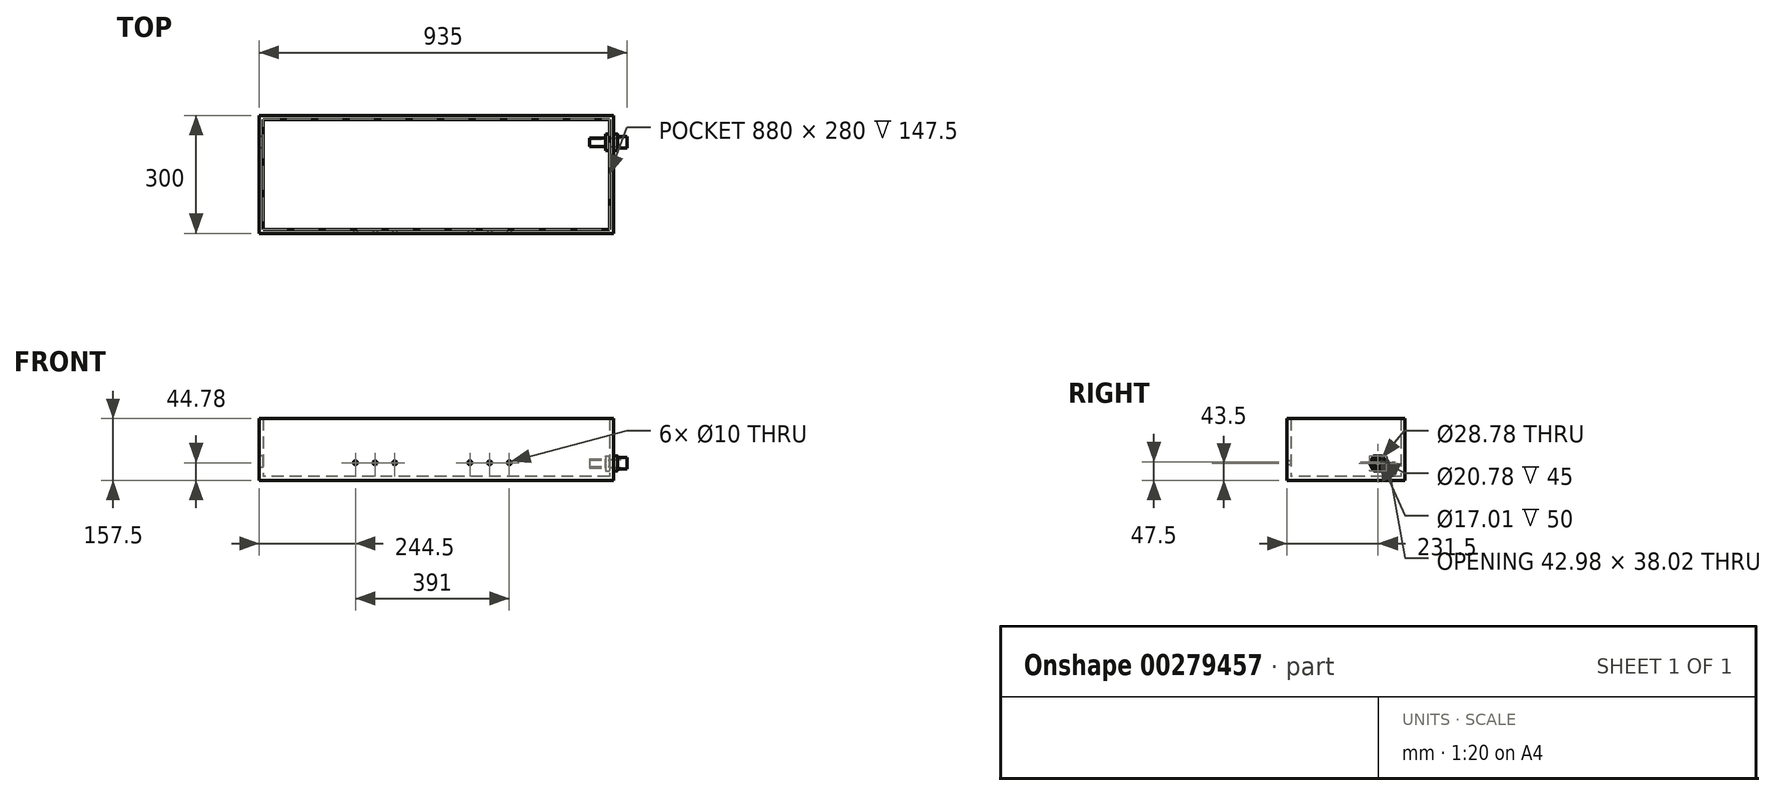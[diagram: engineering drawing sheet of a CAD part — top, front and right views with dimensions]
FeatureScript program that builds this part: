
annotation { "Feature Type Name" : "Feature", "Feature Type Description" : "" }
export const myFeature = defineFeature(function(context is Context, id is Id, definition is map)
    precondition{}
    {
        {
            var Q0;
            Q0=qCreatedBy(makeId("Top.planeOp"),FACE);
            var sketch = newSketch(context, id + "F0", { "sketchPlane" : qUnion([Q0])});
            skLineSegment(sketch, "E0.bottom", {"start": v(450, 150) * mm, "end": v(-450, 150) * mm});
            skLineSegment(sketch, "E0.top", {"start": v(450, -150) * mm, "end": v(-450, -150) * mm});
            skLineSegment(sketch, "E0.left", {"start": v(450, 150) * mm, "end": v(450, -150) * mm});
            skLineSegment(sketch, "E0.right", {"start": v(-450, 150) * mm, "end": v(-450, -150) * mm});
            skPoint(sketch, "E0.middle", {"position": v(0, 0) * mm});
            skSolve(sketch);
        }
        {
            var Q0;
            Q0=qSketchRegion(id+"F0",true);
            extrude(context, id + "F1", {"entities" : qUnion([Q0]), "depth" : 7.5 * mm});
        }
        {
            var Q0;
            Q0=makeQuery(id+"F1.opExtrude","CAP_FACE",FACE,{"disambiguationData":[OSD([sQuery(id+"F0.wireOp",EDGE,"E0.bottom"),sQuery(id+"F0.wireOp",EDGE,"E0.top"),sQuery(id+"F0.wireOp",EDGE,"E0.left"),sQuery(id+"F0.wireOp",EDGE,"E0.right")])],"isStart":false});
            var sketch = newSketch(context, id + "F2", { "sketchPlane" : qUnion([Q0])});
            skLineSegment(sketch, "E1.bottom", {"start": v(442.5, 142.5) * mm, "end": v(-442.5, 142.5) * mm});
            skLineSegment(sketch, "E1.top", {"start": v(442.5, -142.5) * mm, "end": v(-442.5, -142.5) * mm});
            skLineSegment(sketch, "E1.left", {"start": v(442.5, 142.5) * mm, "end": v(442.5, -142.5) * mm});
            skLineSegment(sketch, "E1.right", {"start": v(-442.5, 142.5) * mm, "end": v(-442.5, -142.5) * mm});
            skPoint(sketch, "E1.middle", {"position": v(0, 0) * mm});
            skLineSegment(sketch, "E2.bottom", {"start": v(450, 150) * mm, "end": v(-450, 150) * mm});
            skLineSegment(sketch, "E2.top", {"start": v(450, -150) * mm, "end": v(-450, -150) * mm});
            skLineSegment(sketch, "E2.left", {"start": v(450, 150) * mm, "end": v(450, -150) * mm});
            skLineSegment(sketch, "E2.right", {"start": v(-450, 150) * mm, "end": v(-450, -150) * mm});
            skSolve(sketch);
        }
        {
            var Q0;
            Q0=qSketchRegion(id+"F2",true);
            extrude(context, id + "F3", {"entities" : qUnion([Q0]), "operationType" : NewBodyOperationType.ADD, "depth" : 150 * mm});
        }
        {
            var Q0;
            Q0=makeQuery(id+"F1.opExtrude","CAP_FACE",FACE,{"disambiguationData":[OSD([sQuery(id+"F0.wireOp",EDGE,"E0.bottom"),sQuery(id+"F0.wireOp",EDGE,"E0.top"),sQuery(id+"F0.wireOp",EDGE,"E0.left"),sQuery(id+"F0.wireOp",EDGE,"E0.right")])],"isStart":false});
            extrude(context, id + "F4", {"entities" : qUnion([Q0]), "depth" : 2.5 * mm});
        }
        {
            var Q0;
            Q0=makeQuery(id+"F4.opExtrude","CAP_FACE",FACE,{"disambiguationData":[OSD([sQuery(id+"F0.wireOp",EDGE,"E0.bottom"),sQuery(id+"F0.wireOp",EDGE,"E0.top"),sQuery(id+"F0.wireOp",EDGE,"E0.left"),sQuery(id+"F0.wireOp",EDGE,"E0.right")])],"isStart":false});
            var sketch = newSketch(context, id + "F5", { "sketchPlane" : qUnion([Q0])});
            skLineSegment(sketch, "E3.bottom", {"start": v(442.5, 142.5) * mm, "end": v(-442.5, 142.5) * mm});
            skLineSegment(sketch, "E3.top", {"start": v(442.5, -142.5) * mm, "end": v(-442.5, -142.5) * mm});
            skLineSegment(sketch, "E3.left", {"start": v(442.5, 142.5) * mm, "end": v(442.5, -142.5) * mm});
            skLineSegment(sketch, "E3.right", {"start": v(-442.5, 142.5) * mm, "end": v(-442.5, -142.5) * mm});
            skPoint(sketch, "E3.middle", {"position": v(0, 0) * mm});
            skLineSegment(sketch, "E4.bottom", {"start": v(440, 140) * mm, "end": v(-440, 140) * mm});
            skLineSegment(sketch, "E4.top", {"start": v(440, -140) * mm, "end": v(-440, -140) * mm});
            skLineSegment(sketch, "E4.left", {"start": v(440, 140) * mm, "end": v(440, -140) * mm});
            skLineSegment(sketch, "E4.right", {"start": v(-440, 140) * mm, "end": v(-440, -140) * mm});
            skSolve(sketch);
        }
        {
            var Q0;
            Q0=qSketchRegion(id+"F5",true);
            extrude(context, id + "F6", {"entities" : qUnion([Q0]), "operationType" : NewBodyOperationType.ADD, "depth" : 147.5 * mm});
        }
        {
            var Q0;
            Q0=makeQuery(id+"F3.boolean.opBoolean","MERGE",FACE,{"derivedFrom":[makeQuery(id+"F1.opExtrude","SWEPT_FACE",FACE,{"disambiguationData":[OSD([sQuery(id+"F0.wireOp",EDGE,"E0.top")])]}),makeQuery(id+"F3.opExtrude","SWEPT_FACE",FACE,{"disambiguationData":[OSD([sQuery(id+"F2.wireOp",EDGE,"E2.top")])]})]});
            var sketch = newSketch(context, id + "F7", { "sketchPlane" : qUnion([Q0])});
            skLineSegment(sketch, "E5.bottom", {"start": v(354.25, 147.22) * mm, "end": v(-354.25, 147.22) * mm, "construction": true});
            skLineSegment(sketch, "E5.top", {"start": v(354.25, 15) * mm, "end": v(-354.25, 15) * mm, "construction": true});
            skLineSegment(sketch, "E5.left", {"start": v(354.25, 147.22) * mm, "end": v(354.25, 15) * mm, "construction": true});
            skLineSegment(sketch, "E5.right", {"start": v(-354.25, 147.22) * mm, "end": v(-354.25, 15) * mm, "construction": true});
            skPoint(sketch, "E5.middle", {"position": v(0, 78.75) * mm});
            skPoint(sketch, "E5.middle.positionSnap0", {"position": v(-450, 78.75) * mm});
            skPoint(sketch, "E5.centerSnap0", {"position": v(-450, 78.75) * mm});
            skCircle(sketch, "E6", {"center": v(85.5, 44.78) * mm, "radius": 5 * mm});
            skLineSegment(sketch, "E7", {"start": v(85.5, 44.78) * mm, "end": v(85.5, 15) * mm, "construction": true});
            skLineSegment(sketch, "E8", {"start": v(85.5, 44.78) * mm, "end": v(354.25, 44.78) * mm, "construction": true});
            skCircle(sketch, "E9.1.0.0", {"center": v(135.5, 44.78) * mm, "radius": 5 * mm});
            skLineSegment(sketch, "E9.direction1", {"start": v(85.5, 44.78) * mm, "end": v(135.5, 44.78) * mm, "construction": true});
            skCircle(sketch, "E10", {"center": v(-105.5, 44.78) * mm, "radius": 5 * mm});
            skLineSegment(sketch, "E11", {"start": v(-105.5, 15) * mm, "end": v(-105.5, 44.78) * mm, "construction": true});
            skLineSegment(sketch, "E12", {"start": v(-105.5, 44.78) * mm, "end": v(-354.25, 44.78) * mm, "construction": true});
            skCircle(sketch, "E13.1.0.0", {"center": v(-155.5, 44.78) * mm, "radius": 5 * mm});
            skLineSegment(sketch, "E13.direction1", {"start": v(-105.5, 44.78) * mm, "end": v(-155.5, 44.78) * mm, "construction": true});
            skCircle(sketch, "E14.0.2.0", {"center": v(185.5, 44.78) * mm, "radius": 5 * mm});
            skCircle(sketch, "E15.0.2.0", {"center": v(-205.5, 44.78) * mm, "radius": 5 * mm});
            skSolve(sketch);
        }
        {
            var Q0;
            Q0=qSketchRegion(id+"F7",true);
            extrude(context, id + "F8", {"entities" : qUnion([Q0]), "operationType" : NewBodyOperationType.REMOVE, "oppositeDirection" : true, "depth" : 25 * mm});
        }
        {
            var Q0;
            Q0=makeQuery(id+"F3.boolean.opBoolean","MERGE",FACE,{"derivedFrom":[makeQuery(id+"F1.opExtrude","SWEPT_FACE",FACE,{"disambiguationData":[OSD([sQuery(id+"F0.wireOp",EDGE,"E0.right")])]}),makeQuery(id+"F3.opExtrude","SWEPT_FACE",FACE,{"disambiguationData":[OSD([sQuery(id+"F2.wireOp",EDGE,"E2.right")])]})]});
            var sketch = newSketch(context, id + "F9", { "sketchPlane" : qUnion([Q0])});
            skCircle(sketch, "E16", {"center": v(-81.5, 47.5) * mm, "radius": 14.4 * mm});
            skLineSegment(sketch, "E17", {"start": v(-81.5, 47.5) * mm, "end": v(-81.5, 0) * mm, "construction": true});
            skLineSegment(sketch, "E18", {"start": v(-81.5, 47.5) * mm, "end": v(-150, 47.5) * mm, "construction": true});
            skSolve(sketch);
        }
        {
            var Q0;
            Q0 = qSketchRegion(id + "F9", true);
            extrude(context, id + "F10", {"entities" : qUnion([Q0]), "operationType" : NewBodyOperationType.REMOVE, "oppositeDirection" : true, "depth" : 500 * mm});
        }
        {
            var Q0;
            Q0=makeQuery(id+"F3.boolean.opBoolean","MERGE",FACE,{"derivedFrom":[makeQuery(id+"F1.opExtrude","SWEPT_FACE",FACE,{"disambiguationData":[OSD([sQuery(id+"F0.wireOp",EDGE,"E0.left")])]}),makeQuery(id+"F3.opExtrude","SWEPT_FACE",FACE,{"disambiguationData":[OSD([sQuery(id+"F2.wireOp",EDGE,"E2.left")])]})]});
            var sketch = newSketch(context, id + "F11", { "sketchPlane" : qUnion([Q0])});
            skCircle(sketch, "E19", {"center": v(81.5, 43.5) * mm, "radius": 14.4 * mm});
            skLineSegment(sketch, "E20", {"start": v(81.5, 0) * mm, "end": v(81.5, 43.5) * mm, "construction": true});
            skLineSegment(sketch, "E21", {"start": v(150, 43.5) * mm, "end": v(81.5, 43.5) * mm, "construction": true});
            skSolve(sketch);
        }
        {
            var Q0;
            Q0 = qSketchRegion(id + "F11", true);
            extrude(context, id + "F12", {"entities" : qUnion([Q0]), "operationType" : NewBodyOperationType.REMOVE, "oppositeDirection" : true, "depth" : 25 * mm});
        }
        {
            var Q0;
            Q0=makeQuery(id+"F3.boolean.opBoolean","MERGE",FACE,{"derivedFrom":[makeQuery(id+"F1.opExtrude","SWEPT_FACE",FACE,{"disambiguationData":[OSD([sQuery(id+"F0.wireOp",EDGE,"E0.left")])]}),makeQuery(id+"F3.opExtrude","SWEPT_FACE",FACE,{"disambiguationData":[OSD([sQuery(id+"F2.wireOp",EDGE,"E2.left")])]})]});
            var sketch = newSketch(context, id + "F13", { "sketchPlane" : qUnion([Q0])});
            skCircle(sketch, "E22", {"center": v(81.5, 43.5) * mm, "radius": 10.4 * mm});
            skCircle(sketch, "E23", {"center": v(81.5, 43.5) * mm, "radius": 14.4 * mm});
            skSolve(sketch);
        }
        {
            var Q0;
            Q0 = qSketchRegion(id + "F13", true);
            extrude(context, id + "F14", {"entities" : qUnion([Q0]), "oppositeDirection" : true, "depth" : 10 * mm});
        }
        {
            var Q0;
            Q0=makeQuery(id+"F14.opExtrude","CAP_FACE",FACE,{"disambiguationData":[OSD([sQuery(id+"F13.wireOp",EDGE,"E22"),sQuery(id+"F13.wireOp",EDGE,"E23")])],"isStart":true});
            var sketch = newSketch(context, id + "F15", { "sketchPlane" : qUnion([Q0])});
            skCircle(sketch, "E24.cCircle", {"center": v(81.5, 43.5) * mm, "radius": 19.01 * mm, "construction": true});
            skLineSegment(sketch, "E24.0", {"start": v(72.26, 62.51) * mm, "end": v(90.74, 62.51) * mm});
            skLineSegment(sketch, "E24.1", {"start": v(93.34, 61.01) * mm, "end": v(102.59, 45) * mm});
            skLineSegment(sketch, "E24.2", {"start": v(102.59, 42) * mm, "end": v(93.34, 25.99) * mm});
            skLineSegment(sketch, "E24.3", {"start": v(90.74, 24.49) * mm, "end": v(72.26, 24.49) * mm});
            skLineSegment(sketch, "E24.4", {"start": v(69.66, 25.99) * mm, "end": v(60.41, 42) * mm});
            skLineSegment(sketch, "E24.5", {"start": v(60.41, 45) * mm, "end": v(69.66, 61.01) * mm});
            skPoint(sketch, "E24.0.midPoint", {"position": v(81.5, 62.51) * mm});
            skCircle(sketch, "E25", {"center": v(81.5, 43.5) * mm, "radius": 10.4 * mm});
            skPoint(sketch, "E26.visualSharp", {"position": v(70.52, 62.51) * mm});
            skArc(sketch, "E26.filletArc", {"start": v(72.26, 62.51) * mm, "mid": v(70.76, 62.11) * mm, "end": v(69.66, 61.01) * mm});
            skPoint(sketch, "E27.visualSharp", {"position": v(92.48, 62.51) * mm});
            skArc(sketch, "E27.filletArc", {"start": v(93.34, 61.01) * mm, "mid": v(92.24, 62.11) * mm, "end": v(90.74, 62.51) * mm});
            skPoint(sketch, "E28.visualSharp", {"position": v(103.45, 43.5) * mm});
            skArc(sketch, "E28.filletArc", {"start": v(102.59, 42) * mm, "mid": v(102.99, 43.5) * mm, "end": v(102.59, 45) * mm});
            skPoint(sketch, "E29.visualSharp", {"position": v(92.48, 24.49) * mm});
            skArc(sketch, "E29.filletArc", {"start": v(90.74, 24.49) * mm, "mid": v(92.24, 24.89) * mm, "end": v(93.34, 25.99) * mm});
            skPoint(sketch, "E30.visualSharp", {"position": v(70.52, 24.49) * mm});
            skArc(sketch, "E30.filletArc", {"start": v(69.66, 25.99) * mm, "mid": v(70.76, 24.89) * mm, "end": v(72.26, 24.49) * mm});
            skPoint(sketch, "E31.visualSharp", {"position": v(59.55, 43.5) * mm});
            skArc(sketch, "E31.filletArc", {"start": v(60.41, 45) * mm, "mid": v(60.01, 43.5) * mm, "end": v(60.41, 42) * mm});
            skSolve(sketch);
        }
        {
            var Q0;
            Q0 = qSketchRegion(id + "F15", true);
            extrude(context, id + "F16", {"entities" : qUnion([Q0]), "operationType" : NewBodyOperationType.ADD, "depth" : 10 * mm});
        }
        {
            var Q0;
            Q0=makeQuery(id+"F16.opExtrude","CAP_FACE",FACE,{"disambiguationData":[OSD([sQuery(id+"F15.wireOp",EDGE,"E24.0"),sQuery(id+"F15.wireOp",EDGE,"E24.1"),sQuery(id+"F15.wireOp",EDGE,"E24.2"),sQuery(id+"F15.wireOp",EDGE,"E24.3"),sQuery(id+"F15.wireOp",EDGE,"E24.4"),sQuery(id+"F15.wireOp",EDGE,"E24.5"),sQuery(id+"F15.wireOp",EDGE,"E25"),sQuery(id+"F15.wireOp",EDGE,"E26.filletArc"),sQuery(id+"F15.wireOp",EDGE,"E27.filletArc"),sQuery(id+"F15.wireOp",EDGE,"E28.filletArc"),sQuery(id+"F15.wireOp",EDGE,"E29.filletArc"),sQuery(id+"F15.wireOp",EDGE,"E30.filletArc"),sQuery(id+"F15.wireOp",EDGE,"E31.filletArc")])],"isStart":false});
            var sketch = newSketch(context, id + "F17", { "sketchPlane" : qUnion([Q0])});
            skCircle(sketch, "E32", {"center": v(81.5, 43.5) * mm, "radius": 14.62 * mm});
            skCircle(sketch, "E33", {"center": v(81.5, 43.5) * mm, "radius": 10.4 * mm});
            skSolve(sketch);
        }
        {
            var Q0;
            Q0 = qSketchRegion(id + "F17", true);
            extrude(context, id + "F18", {"entities" : qUnion([Q0]), "operationType" : NewBodyOperationType.ADD, "depth" : 25 * mm});
        }
        {
            var Q0;
            Q0=makeQuery(id+"F14.opExtrude","CAP_FACE",FACE,{"disambiguationData":[OSD([sQuery(id+"F13.wireOp",EDGE,"E22"),sQuery(id+"F13.wireOp",EDGE,"E23")])],"isStart":false});
            var sketch = newSketch(context, id + "F19", { "sketchPlane" : qUnion([Q0])});
            skCircle(sketch, "E34", {"center": v(-81.5, 43.5) * mm, "radius": 8.5 * mm});
            skCircle(sketch, "E35", {"center": v(-81.5, 43.5) * mm, "radius": 11.24 * mm});
            skSolve(sketch);
        }
        {
            var Q0;
            Q0 = qSketchRegion(id + "F19", true);
            extrude(context, id + "F20", {"entities" : qUnion([Q0]), "operationType" : NewBodyOperationType.ADD, "depth" : 50 * mm});
        }
        {
            var Q0;
            Q0=makeQuery(id+"F14.opExtrude","CAP_FACE",FACE,{"disambiguationData":[OSD([sQuery(id+"F13.wireOp",EDGE,"E22"),sQuery(id+"F13.wireOp",EDGE,"E23")])],"isStart":false});
            var sketch = newSketch(context, id + "F21", { "sketchPlane" : qUnion([Q0])});
            skCircle(sketch, "E36.cCircle", {"center": v(-81.5, 43.5) * mm, "radius": 19.01 * mm, "construction": true});
            skLineSegment(sketch, "E36.0", {"start": v(-90.74, 62.51) * mm, "end": v(-72.26, 62.51) * mm});
            skLineSegment(sketch, "E36.1", {"start": v(-69.66, 61.01) * mm, "end": v(-60.41, 45) * mm});
            skLineSegment(sketch, "E36.2", {"start": v(-60.41, 42) * mm, "end": v(-69.66, 25.99) * mm});
            skLineSegment(sketch, "E36.3", {"start": v(-72.26, 24.49) * mm, "end": v(-90.74, 24.49) * mm});
            skLineSegment(sketch, "E36.4", {"start": v(-93.34, 25.99) * mm, "end": v(-102.59, 42) * mm});
            skLineSegment(sketch, "E36.5", {"start": v(-102.59, 45) * mm, "end": v(-93.34, 61.01) * mm});
            skPoint(sketch, "E36.0.midPoint", {"position": v(-81.5, 62.51) * mm});
            skPoint(sketch, "E37.visualSharp", {"position": v(-92.48, 62.51) * mm});
            skArc(sketch, "E37.filletArc", {"start": v(-90.74, 62.51) * mm, "mid": v(-92.24, 62.11) * mm, "end": v(-93.34, 61.01) * mm});
            skPoint(sketch, "E38.visualSharp", {"position": v(-70.52, 62.51) * mm});
            skArc(sketch, "E38.filletArc", {"start": v(-69.66, 61.01) * mm, "mid": v(-70.76, 62.11) * mm, "end": v(-72.26, 62.51) * mm});
            skPoint(sketch, "E39.visualSharp", {"position": v(-59.55, 43.5) * mm});
            skArc(sketch, "E39.filletArc", {"start": v(-60.41, 42) * mm, "mid": v(-60.01, 43.5) * mm, "end": v(-60.41, 45) * mm});
            skPoint(sketch, "E40.visualSharp", {"position": v(-70.52, 24.49) * mm});
            skArc(sketch, "E40.filletArc", {"start": v(-72.26, 24.49) * mm, "mid": v(-70.76, 24.89) * mm, "end": v(-69.66, 25.99) * mm});
            skPoint(sketch, "E41.visualSharp", {"position": v(-92.48, 24.49) * mm});
            skArc(sketch, "E41.filletArc", {"start": v(-93.34, 25.99) * mm, "mid": v(-92.24, 24.89) * mm, "end": v(-90.74, 24.49) * mm});
            skPoint(sketch, "E42.visualSharp", {"position": v(-103.45, 43.5) * mm});
            skArc(sketch, "E42.filletArc", {"start": v(-102.59, 45) * mm, "mid": v(-102.99, 43.5) * mm, "end": v(-102.59, 42) * mm});
            skCircle(sketch, "E43", {"center": v(-81.5, 43.5) * mm, "radius": 11.24 * mm});
            skSolve(sketch);
        }
        {
            var Q0;
            Q0 = qSketchRegion(id + "F21", true);
            extrude(context, id + "F22", {"entities" : qUnion([Q0]), "operationType" : NewBodyOperationType.ADD, "depth" : 10 * mm});
        }
    });
